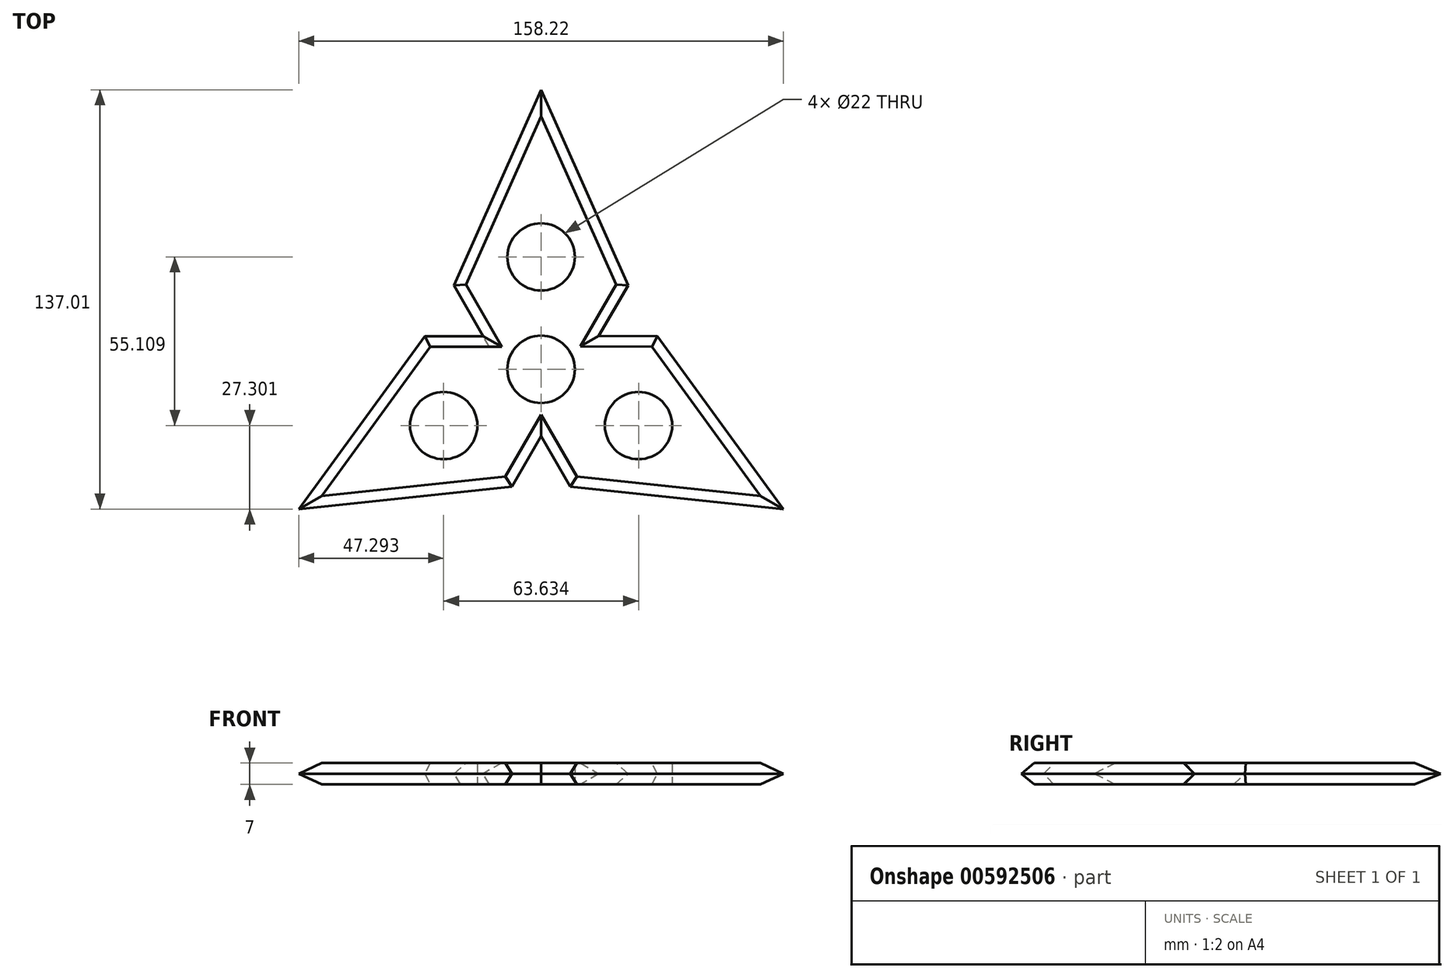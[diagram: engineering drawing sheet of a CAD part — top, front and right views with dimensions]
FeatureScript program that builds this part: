
annotation { "Feature Type Name" : "Feature", "Feature Type Description" : "" }
export const myFeature = defineFeature(function(context is Context, id is Id, definition is map)
    precondition{}
    {
        {
            var Q0;
            Q0=qCreatedBy(makeId("Top.planeOp"),FACE);
            var sketch = newSketch(context, id + "F0", { "sketchPlane" : qUnion([Q0])});
            skCircle(sketch, "E0", {"center": v(0, 0) * mm, "radius": 11 * mm});
            skCircle(sketch, "E1", {"center": v(0, 36.74) * mm, "radius": 11 * mm});
            skLineSegment(sketch, "E2", {"start": v(0.01, -32.8) * mm, "end": v(0, -32.8) * mm});
            skLineSegment(sketch, "E3.MirrorCS", {"start": v(28.4, 16.41) * mm, "end": v(28.4, 16.42) * mm});
            skCircle(sketch, "E4.1.0", {"center": v(-31.82, -18.37) * mm, "radius": 11 * mm});
            skLineSegment(sketch, "E4.1.1", {"start": v(-28.41, 16.39) * mm, "end": v(-28.42, 16.38) * mm});
            skLineSegment(sketch, "E4.1.2", {"start": v(28.4, 16.41) * mm, "end": v(28.4, 16.4) * mm});
            skCircle(sketch, "E4.2.0", {"center": v(31.82, -18.37) * mm, "radius": 11 * mm});
            skLineSegment(sketch, "E4.2.1", {"start": v(0.01, -32.8) * mm, "end": v(0.03, -32.8) * mm});
            skLineSegment(sketch, "E4.2.2", {"start": v(-28.41, 16.39) * mm, "end": v(-28.4, 16.4) * mm});
            skPoint(sketch, "E5.orphan", {"position": v(-0.03, 91.42) * mm});
            skLineSegment(sketch, "E6", {"start": v(-0.03, 91.42) * mm, "end": v(28.4, 27.46) * mm});
            skPoint(sketch, "E7.end.orphan", {"position": v(42.28, 16.4) * mm});
            skPoint(sketch, "E8.orphan", {"position": v(-79.16, -45.74) * mm});
            skPoint(sketch, "E9.orphan", {"position": v(79.2, -45.68) * mm});
            skLineSegment(sketch, "E10.1.0", {"start": v(-79.16, -45.74) * mm, "end": v(-37.97, 10.86) * mm});
            skLineSegment(sketch, "E10.2.0", {"start": v(79.2, -45.68) * mm, "end": v(9.58, -38.31) * mm});
            skLineSegment(sketch, "E11.MirrorCS", {"start": v(-79.2, -45.68) * mm, "end": v(-9.58, -38.31) * mm});
            skLineSegment(sketch, "E12.1.0", {"start": v(79.16, -45.74) * mm, "end": v(37.97, 10.86) * mm});
            skLineSegment(sketch, "E12.2.0", {"start": v(0.03, 91.42) * mm, "end": v(-28.4, 27.46) * mm});
            skLineSegment(sketch, "E13", {"start": v(-28.4, 27.46) * mm, "end": v(-18.9, 10.86) * mm});
            skLineSegment(sketch, "E14", {"start": v(-37.97, 10.86) * mm, "end": v(-18.9, 10.86) * mm});
            skLineSegment(sketch, "E15.1.0", {"start": v(-9.58, -38.31) * mm, "end": v(0.04, -21.79) * mm});
            skLineSegment(sketch, "E15.1.1", {"start": v(9.58, -38.31) * mm, "end": v(0.04, -21.79) * mm});
            skLineSegment(sketch, "E15.2.0", {"start": v(37.97, 10.86) * mm, "end": v(18.85, 10.93) * mm});
            skLineSegment(sketch, "E15.2.1", {"start": v(28.4, 27.46) * mm, "end": v(18.85, 10.93) * mm});
            skSolve(sketch);
        }
        {
            var Q0;
            Q0=makeQuery(id+"F0.imprint","IMPRINT",FACE,{"disambiguationData":[TD([[makeQuery(id+"F0.imprint","IMPRINT",EDGE,{"derivedFrom":sQuery(id+"F0.wireOp",EDGE,"E0")}),-1.0]])]});
            extrude(context, id + "F1", {"entities" : qUnion([Q0]), "depth" : 7 * mm, "offsetDistance" : 25 * mm});
        }
        {
            var Q0;
            Q0=makeQuery(id+"F1.opExtrude","CAP_EDGE",EDGE,{"disambiguationData":[OSD([sQuery(id+"F0.wireOp",EDGE,"E11.MirrorCS")])],"isStart":false});
            var Q1;
            Q1=makeQuery(id+"F1.opExtrude","CAP_EDGE",EDGE,{"disambiguationData":[OSD([sQuery(id+"F0.wireOp",EDGE,"E15.1.0")])],"isStart":true});
            var Q2;
            Q2=makeQuery(id+"F1.opExtrude","CAP_EDGE",EDGE,{"disambiguationData":[OSD([sQuery(id+"F0.wireOp",EDGE,"E11.MirrorCS")])],"isStart":true});
            var Q3;
            Q3=makeQuery(id+"F1.opExtrude","CAP_EDGE",EDGE,{"disambiguationData":[OSD([sQuery(id+"F0.wireOp",EDGE,"E15.1.0")])],"isStart":false});
            var Q4;
            Q4=makeQuery(id+"F1.opExtrude","CAP_EDGE",EDGE,{"disambiguationData":[OSD([sQuery(id+"F0.wireOp",EDGE,"E15.1.1")])],"isStart":false});
            var Q5;
            Q5=makeQuery(id+"F1.opExtrude","CAP_EDGE",EDGE,{"disambiguationData":[OSD([sQuery(id+"F0.wireOp",EDGE,"E15.1.1")])],"isStart":true});
            var Q6;
            Q6=makeQuery(id+"F1.opExtrude","CAP_EDGE",EDGE,{"disambiguationData":[OSD([sQuery(id+"F0.wireOp",EDGE,"E10.2.0")])],"isStart":false});
            var Q7;
            Q7=makeQuery(id+"F1.opExtrude","CAP_EDGE",EDGE,{"disambiguationData":[OSD([sQuery(id+"F0.wireOp",EDGE,"E10.2.0")])],"isStart":true});
            var Q8;
            Q8=makeQuery(id+"F1.opExtrude","CAP_EDGE",EDGE,{"disambiguationData":[OSD([sQuery(id+"F0.wireOp",EDGE,"E10.1.0")])],"isStart":false});
            var Q9;
            Q9=makeQuery(id+"F1.opExtrude","CAP_EDGE",EDGE,{"disambiguationData":[OSD([sQuery(id+"F0.wireOp",EDGE,"E12.1.0")])],"isStart":false});
            var Q10;
            Q10=makeQuery(id+"F1.opExtrude","CAP_EDGE",EDGE,{"disambiguationData":[OSD([sQuery(id+"F0.wireOp",EDGE,"E12.2.0")])],"isStart":false});
            var Q11;
            Q11=makeQuery(id+"F1.opExtrude","CAP_EDGE",EDGE,{"disambiguationData":[OSD([sQuery(id+"F0.wireOp",EDGE,"E6")])],"isStart":false});
            var Q12;
            Q12=makeQuery(id+"F1.opExtrude","CAP_EDGE",EDGE,{"disambiguationData":[OSD([sQuery(id+"F0.wireOp",EDGE,"E14")])],"isStart":false});
            var Q13;
            Q13=makeQuery(id+"F1.opExtrude","CAP_EDGE",EDGE,{"disambiguationData":[OSD([sQuery(id+"F0.wireOp",EDGE,"E13")])],"isStart":false});
            var Q14;
            Q14=makeQuery(id+"F1.opExtrude","CAP_EDGE",EDGE,{"disambiguationData":[OSD([sQuery(id+"F0.wireOp",EDGE,"E15.2.1")])],"isStart":true});
            var Q15;
            Q15=makeQuery(id+"F1.opExtrude","CAP_EDGE",EDGE,{"disambiguationData":[OSD([sQuery(id+"F0.wireOp",EDGE,"E15.2.0")])],"isStart":false});
            var Q16;
            Q16=makeQuery(id+"F1.opExtrude","CAP_EDGE",EDGE,{"disambiguationData":[OSD([sQuery(id+"F0.wireOp",EDGE,"E15.2.1")])],"isStart":false});
            var Q17;
            Q17=makeQuery(id+"F1.opExtrude","CAP_EDGE",EDGE,{"disambiguationData":[OSD([sQuery(id+"F0.wireOp",EDGE,"E14")])],"isStart":true});
            var Q18;
            Q18=makeQuery(id+"F1.opExtrude","CAP_EDGE",EDGE,{"disambiguationData":[OSD([sQuery(id+"F0.wireOp",EDGE,"E10.1.0")])],"isStart":true});
            var Q19;
            Q19=makeQuery(id+"F1.opExtrude","CAP_EDGE",EDGE,{"disambiguationData":[OSD([sQuery(id+"F0.wireOp",EDGE,"E12.2.0")])],"isStart":true});
            var Q20;
            Q20=makeQuery(id+"F1.opExtrude","CAP_EDGE",EDGE,{"disambiguationData":[OSD([sQuery(id+"F0.wireOp",EDGE,"E6")])],"isStart":true});
            var Q21;
            Q21=makeQuery(id+"F1.opExtrude","CAP_EDGE",EDGE,{"disambiguationData":[OSD([sQuery(id+"F0.wireOp",EDGE,"E12.1.0")])],"isStart":true});
            var Q22;
            Q22=makeQuery(id+"F1.opExtrude","CAP_EDGE",EDGE,{"disambiguationData":[OSD([sQuery(id+"F0.wireOp",EDGE,"E15.2.0")])],"isStart":true});
            chamfer(context, id + "F2", {"entities" : qUnion([Q0, Q1, Q2, Q3, Q4, Q5, Q6, Q7, Q8, Q9, Q10, Q11, Q12, Q13, Q14, Q15, Q16, Q17, Q18, Q19, Q20, Q21, Q22]), "width" : 3.5 * mm, "tangentPropagation" : true});
        }
    });
